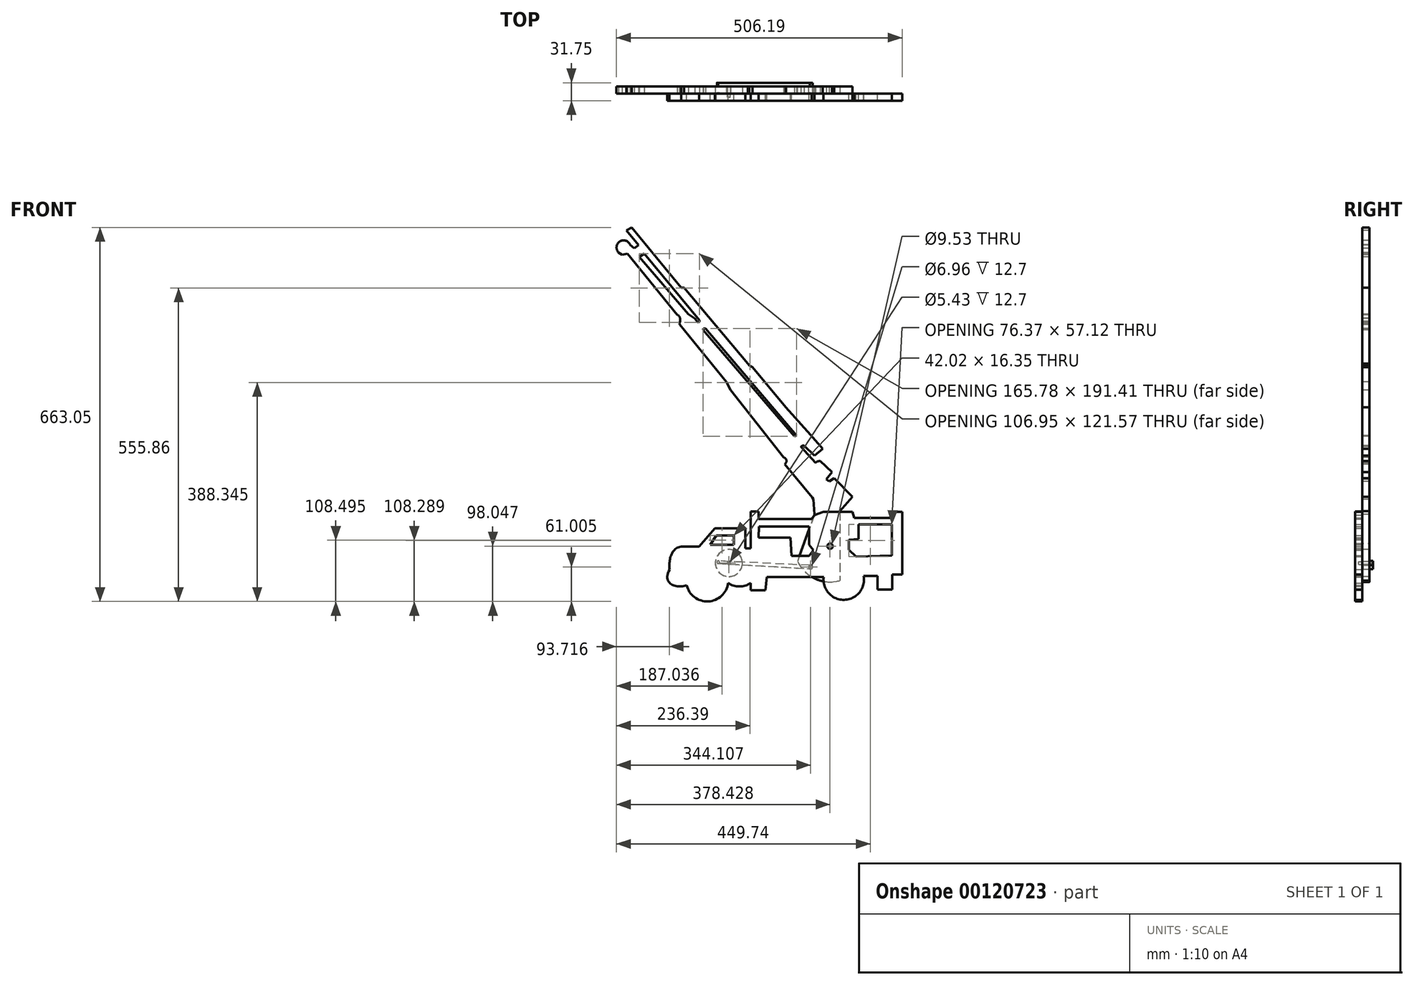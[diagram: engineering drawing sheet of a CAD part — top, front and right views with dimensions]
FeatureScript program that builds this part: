
annotation { "Feature Type Name" : "Feature", "Feature Type Description" : "" }
export const myFeature = defineFeature(function(context is Context, id is Id, definition is map)
    precondition{}
    {
        {
            var Q0;
            Q0=qCreatedBy(makeId("Front.planeOp"),FACE);
            var sketch = newSketch(context, id + "F0", { "sketchPlane" : qUnion([Q0])});
            skLineSegment(sketch, "E0", {"start": v(-70.97, -268.37) * mm, "end": v(-14.7, -268.37) * mm});
            skLineSegment(sketch, "E1", {"start": v(-14.7, -268.37) * mm, "end": v(-12.8, -300.2) * mm});
            skLineSegment(sketch, "E2", {"start": v(-12.8, -300.2) * mm, "end": v(18.8, -300.2) * mm});
            skLineSegment(sketch, "E3", {"start": v(18.8, -300.2) * mm, "end": v(25.92, -290.22) * mm});
            skLineSegment(sketch, "E4", {"start": v(25.92, -290.22) * mm, "end": v(18.8, -280.72) * mm});
            skLineSegment(sketch, "E5", {"start": v(18.8, -280.72) * mm, "end": v(18.8, -248.42) * mm});
            skLineSegment(sketch, "E6", {"start": v(18.8, -248.42) * mm, "end": v(-70.5, -248.42) * mm});
            skLineSegment(sketch, "E7", {"start": v(-70.5, -248.42) * mm, "end": v(-70.97, -268.37) * mm});
            skLineSegment(sketch, "E8", {"start": v(-176.17, -284.05) * mm, "end": v(-148.62, -251.27) * mm});
            skLineSegment(sketch, "E9", {"start": v(-148.62, -251.27) * mm, "end": v(-94.72, -251.27) * mm});
            skLineSegment(sketch, "E10", {"start": v(-94.72, -251.27) * mm, "end": v(-94.72, -287.37) * mm});
            skLineSegment(sketch, "E11", {"start": v(-94.72, -287.37) * mm, "end": v(-84.98, -287.37) * mm});
            skLineSegment(sketch, "E12", {"start": v(-84.98, -287.37) * mm, "end": v(-84.98, -221.83) * mm});
            skLineSegment(sketch, "E13", {"start": v(-84.98, -221.83) * mm, "end": v(-70.97, -221.83) * mm});
            skLineSegment(sketch, "E14", {"start": v(-70.97, -221.83) * mm, "end": v(-70.97, -234.89) * mm});
            skLineSegment(sketch, "E15", {"start": v(-70.97, -234.89) * mm, "end": v(22.83, -234.89) * mm});
            skLineSegment(sketch, "E16", {"start": v(22.83, -234.89) * mm, "end": v(28.3, -228) * mm});
            skLineSegment(sketch, "E17", {"start": v(28.3, -228) * mm, "end": v(44.2, -222.3) * mm});
            skLineSegment(sketch, "E18", {"start": v(44.2, -222.3) * mm, "end": v(95.5, -222.3) * mm});
            skLineSegment(sketch, "E19", {"start": v(95.5, -222.3) * mm, "end": v(98.58, -233.46) * mm});
            skLineSegment(sketch, "E20", {"start": v(98.58, -233.46) * mm, "end": v(165.08, -233.46) * mm});
            skLineSegment(sketch, "E21", {"start": v(165.08, -233.46) * mm, "end": v(165.08, -222.07) * mm});
            skLineSegment(sketch, "E22", {"start": v(165.08, -222.07) * mm, "end": v(183.43, -222.07) * mm});
            skLineSegment(sketch, "E23", {"start": v(183.43, -222.07) * mm, "end": v(183.43, -333.2) * mm});
            skLineSegment(sketch, "E24", {"start": v(183.43, -333.2) * mm, "end": v(165.79, -333.2) * mm});
            skLineSegment(sketch, "E25", {"start": v(165.79, -333.2) * mm, "end": v(165.79, -360.27) * mm});
            skLineSegment(sketch, "E26", {"start": v(165.79, -360.27) * mm, "end": v(139.9, -360.27) * mm});
            skLineSegment(sketch, "E27", {"start": v(139.9, -360.27) * mm, "end": v(139.9, -336.29) * mm});
            skLineSegment(sketch, "E28", {"start": v(139.9, -336.29) * mm, "end": v(115.2, -336.29) * mm});
            skLineSegment(sketch, "E29", {"start": v(44.44, -338.19) * mm, "end": v(-56.49, -338.19) * mm});
            skLineSegment(sketch, "E30", {"start": v(-56.49, -338.19) * mm, "end": v(-58.86, -361.43) * mm});
            skLineSegment(sketch, "E31", {"start": v(-58.86, -361.43) * mm, "end": v(-85.03, -361.43) * mm});
            skLineSegment(sketch, "E32", {"start": v(-85.03, -361.43) * mm, "end": v(-85.03, -348.85) * mm});
            skLineSegment(sketch, "E33", {"start": v(-208.06, -283.94) * mm, "end": v(-176.17, -284.05) * mm});
            skLineSegment(sketch, "E34", {"start": v(-156.73, -280.67) * mm, "end": v(-146.16, -264.57) * mm});
            skLineSegment(sketch, "E35", {"start": v(-146.16, -264.57) * mm, "end": v(-114.72, -264.57) * mm});
            skLineSegment(sketch, "E36", {"start": v(-114.72, -264.57) * mm, "end": v(-114.72, -280.92) * mm});
            skLineSegment(sketch, "E37", {"start": v(-114.72, -280.92) * mm, "end": v(-156.73, -280.67) * mm});
            skLineSegment(sketch, "E38", {"start": v(165.17, -244.4) * mm, "end": v(165.17, -299.82) * mm});
            skLineSegment(sketch, "E39", {"start": v(165.17, -299.82) * mm, "end": v(101.49, -301.51) * mm});
            skLineSegment(sketch, "E40", {"start": v(101.49, -301.51) * mm, "end": v(88.8, -289.45) * mm});
            skLineSegment(sketch, "E41", {"start": v(88.8, -289.45) * mm, "end": v(88.8, -272.1) * mm});
            skLineSegment(sketch, "E42", {"start": v(88.8, -272.1) * mm, "end": v(106.14, -270.41) * mm});
            skLineSegment(sketch, "E43", {"start": v(106.14, -270.41) * mm, "end": v(106.14, -244.4) * mm});
            skLineSegment(sketch, "E44", {"start": v(106.14, -244.4) * mm, "end": v(165.17, -244.4) * mm});
            skArc(sketch, "E45", {"start": v(44.44, -338.19) * mm, "mid": v(80.93, -378.42) * mm, "end": v(115.2, -336.29) * mm});
            skArc(sketch, "E46", {"start": v(-199, -348.85) * mm, "mid": v(-162.01, -381.24) * mm, "end": v(-125.03, -348.85) * mm});
            skArc(sketch, "E47", {"start": v(-125.03, -348.85) * mm, "mid": v(-105.03, -354.54) * mm, "end": v(-85.03, -348.85) * mm});
            skFitSpline(sketch, "E48", {"points": [v(-208.06, -283.94) * mm, v(-228.69, -324.45) * mm], "startDerivative": vector(-59.8, -8.02) * mm, "endDerivative": vector(5.3, -34.5) * mm});
            skFitSpline(sketch, "E49", {"points": [v(-198.37, -352.3) * mm, v(-228.69, -324.45) * mm], "startDerivative": vector(-50.07, -20.1) * mm, "endDerivative": vector(43.3, 82.5) * mm});
            skLineSegment(sketch, "E50", {"start": v(-305.5, 276.53) * mm, "end": v(-295.52, 281.81) * mm});
            skLineSegment(sketch, "E51", {"start": v(-295.52, 281.81) * mm, "end": v(-208.1, 175.03) * mm});
            skLineSegment(sketch, "E52", {"start": v(-208.1, 175.03) * mm, "end": v(-203.24, 175.03) * mm});
            skLineSegment(sketch, "E53", {"start": v(-203.24, 175.03) * mm, "end": v(-90.29, 40.23) * mm});
            skLineSegment(sketch, "E54", {"start": v(-90.29, 40.23) * mm, "end": v(-87.44, 37.62) * mm});
            skLineSegment(sketch, "E55", {"start": v(-87.44, 37.62) * mm, "end": v(-81.5, 34.05) * mm});
            skLineSegment(sketch, "E56", {"start": v(-81.5, 34.05) * mm, "end": v(-22.51, -37.08) * mm});
            skLineSegment(sketch, "E57", {"start": v(-22.51, -37.08) * mm, "end": v(20.91, -85.9) * mm});
            skLineSegment(sketch, "E58", {"start": v(20.91, -85.9) * mm, "end": v(42.79, -110.3) * mm});
            skLineSegment(sketch, "E59", {"start": v(42.79, -110.3) * mm, "end": v(27.97, -122.45) * mm});
            skLineSegment(sketch, "E60", {"start": v(27.97, -122.45) * mm, "end": v(9.4, -104.62) * mm});
            skLineSegment(sketch, "E61", {"start": v(9.4, -104.62) * mm, "end": v(4.22, -107) * mm});
            skLineSegment(sketch, "E62", {"start": v(4.22, -107) * mm, "end": v(29.81, -135.31) * mm});
            skLineSegment(sketch, "E63", {"start": v(38.4, -132.45) * mm, "end": v(59.47, -152.17) * mm});
            skLineSegment(sketch, "E64", {"start": v(59.47, -152.17) * mm, "end": v(49.15, -164.34) * mm});
            skLineSegment(sketch, "E65", {"start": v(49.15, -164.34) * mm, "end": v(54.1, -168.54) * mm});
            skLineSegment(sketch, "E66", {"start": v(54.1, -168.54) * mm, "end": v(63.2, -162.72) * mm});
            skLineSegment(sketch, "E67", {"start": v(63.2, -162.72) * mm, "end": v(95.33, -195.57) * mm});
            skLineSegment(sketch, "E68", {"start": v(95.33, -195.57) * mm, "end": v(72.9, -221.17) * mm});
            skLineSegment(sketch, "E69", {"start": v(72.9, -221.17) * mm, "end": v(43.7, -221.17) * mm});
            skLineSegment(sketch, "E70", {"start": v(43.7, -221.17) * mm, "end": v(28.16, -226.67) * mm});
            skLineSegment(sketch, "E71", {"start": v(28.16, -226.67) * mm, "end": v(26.25, -200.01) * mm});
            skLineSegment(sketch, "E72", {"start": v(26.25, -200.01) * mm, "end": v(24.24, -197.16) * mm});
            skLineSegment(sketch, "E73", {"start": v(24.24, -197.16) * mm, "end": v(-24.88, -137.93) * mm});
            skLineSegment(sketch, "E74", {"start": v(-26.67, -125.71) * mm, "end": v(-120.23, -6.25) * mm});
            skLineSegment(sketch, "E75", {"start": v(-120.23, -6.25) * mm, "end": v(-128.07, 7.99) * mm});
            skLineSegment(sketch, "E76", {"start": v(-128.07, 7.99) * mm, "end": v(-210.4, 110.04) * mm});
            skLineSegment(sketch, "E77", {"start": v(-210.4, 110.04) * mm, "end": v(-211, 112.1) * mm});
            skLineSegment(sketch, "E78", {"start": v(-211, 112.1) * mm, "end": v(-210.26, 115.3) * mm});
            skLineSegment(sketch, "E79", {"start": v(-210.26, 115.3) * mm, "end": v(-210.26, 121.03) * mm});
            skLineSegment(sketch, "E80", {"start": v(-214.9, 127.1) * mm, "end": v(-303.36, 235.3) * mm});
            skLineSegment(sketch, "E81", {"start": v(-303.36, 235.3) * mm, "end": v(-312.78, 233.5) * mm});
            skLineSegment(sketch, "E82", {"start": v(-312.78, 233.5) * mm, "end": v(-319.05, 237.54) * mm});
            skLineSegment(sketch, "E83", {"start": v(-298.66, 251.66) * mm, "end": v(-291.04, 244.71) * mm});
            skLineSegment(sketch, "E84", {"start": v(-291.04, 244.71) * mm, "end": v(-283.64, 250.54) * mm});
            skLineSegment(sketch, "E85", {"start": v(-283.64, 250.54) * mm, "end": v(-305.5, 276.53) * mm});
            skLineSegment(sketch, "E86", {"start": v(-282.52, 230.03) * mm, "end": v(-273.33, 235.4) * mm});
            skLineSegment(sketch, "E87", {"start": v(-273.33, 235.4) * mm, "end": v(-176.05, 117.36) * mm});
            skLineSegment(sketch, "E88", {"start": v(-179.39, 114.6) * mm, "end": v(-184.03, 120.25) * mm});
            skLineSegment(sketch, "E89", {"start": v(-184.03, 120.25) * mm, "end": v(-195.62, 127.85) * mm});
            skLineSegment(sketch, "E90", {"start": v(-195.62, 127.85) * mm, "end": v(-282.52, 230.03) * mm});
            skLineSegment(sketch, "E91", {"start": v(-165.1, 102.8) * mm, "end": v(-3.48, -87.22) * mm});
            skLineSegment(sketch, "E92", {"start": v(-3.48, -87.22) * mm, "end": v(-7.74, -88.6) * mm});
            skLineSegment(sketch, "E93", {"start": v(-7.74, -88.6) * mm, "end": v(-169.26, 100.29) * mm});
            skLineSegment(sketch, "E94", {"start": v(-169.26, 100.29) * mm, "end": v(-168.67, 102.8) * mm});
            skLineSegment(sketch, "E95", {"start": v(-168.67, 102.8) * mm, "end": v(-165.1, 102.8) * mm});
            skArc(sketch, "E96", {"start": v(-24.88, -137.93) * mm, "mid": v(-21.64, -131.22) * mm, "end": v(-26.67, -125.71) * mm});
            skArc(sketch, "E97", {"start": v(38.4, -132.45) * mm, "mid": v(33.76, -132.83) * mm, "end": v(29.81, -135.31) * mm});
            skArc(sketch, "E98", {"start": v(9.4, -104.62) * mm, "mid": v(6.53, -105.2) * mm, "end": v(4.22, -107) * mm});
            skArc(sketch, "E99", {"start": v(-179.39, 114.6) * mm, "mid": v(-176.35, 114.32) * mm, "end": v(-176.05, 117.36) * mm});
            skArc(sketch, "E100", {"start": v(-210.26, 121.03) * mm, "mid": v(-211.84, 124.63) * mm, "end": v(-214.9, 127.1) * mm});
            skArc(sketch, "E101", {"start": v(-298.66, 251.66) * mm, "mid": v(-317.33, 256.85) * mm, "end": v(-319.05, 237.54) * mm});
            skSolve(sketch);
        }
        {
            var Q0;
            Q0=makeQuery(id+"F0.imprint","IMPRINT",FACE,{"disambiguationData":[TD([[makeQuery(id+"F0.imprint","IMPRINT",EDGE,{"derivedFrom":sQuery(id+"F0.wireOp",EDGE,"E0")}),-1.0]])]});
            extrude(context, id + "F1", {"entities" : qUnion([Q0]), "depth" : 12.7 * mm});
        }
        {
            var Q0;
            Q0=makeQuery(id+"F0.imprint","IMPRINT",FACE,{"disambiguationData":[TD([[makeQuery(id+"F0.imprint","IMPRINT",EDGE,{"derivedFrom":sQuery(id+"F0.wireOp",EDGE,"E50")}),-1.0]])]});
            extrude(context, id + "F2", {"entities" : qUnion([Q0]), "oppositeDirection" : true, "depth" : 12.7 * mm});
        }
        {
            var Q0;
            Q0=makeQuery(id+"F2.opExtrude","CAP_FACE",FACE,{"disambiguationData":[OSD([sQuery(id+"F0.wireOp",EDGE,"E50"),sQuery(id+"F0.wireOp",EDGE,"E51"),sQuery(id+"F0.wireOp",EDGE,"E52"),sQuery(id+"F0.wireOp",EDGE,"E53"),sQuery(id+"F0.wireOp",EDGE,"E54"),sQuery(id+"F0.wireOp",EDGE,"E55"),sQuery(id+"F0.wireOp",EDGE,"E56"),sQuery(id+"F0.wireOp",EDGE,"E57"),sQuery(id+"F0.wireOp",EDGE,"E58"),sQuery(id+"F0.wireOp",EDGE,"E59"),sQuery(id+"F0.wireOp",EDGE,"E60"),sQuery(id+"F0.wireOp",EDGE,"E62"),sQuery(id+"F0.wireOp",EDGE,"E63"),sQuery(id+"F0.wireOp",EDGE,"E64"),sQuery(id+"F0.wireOp",EDGE,"E65"),sQuery(id+"F0.wireOp",EDGE,"E66"),sQuery(id+"F0.wireOp",EDGE,"E67"),sQuery(id+"F0.wireOp",EDGE,"E68"),sQuery(id+"F0.wireOp",EDGE,"E69"),sQuery(id+"F0.wireOp",EDGE,"E70"),sQuery(id+"F0.wireOp",EDGE,"E71"),sQuery(id+"F0.wireOp",EDGE,"E72"),sQuery(id+"F0.wireOp",EDGE,"E73"),sQuery(id+"F0.wireOp",EDGE,"E74"),sQuery(id+"F0.wireOp",EDGE,"E75"),sQuery(id+"F0.wireOp",EDGE,"E76"),sQuery(id+"F0.wireOp",EDGE,"E77"),sQuery(id+"F0.wireOp",EDGE,"E78"),sQuery(id+"F0.wireOp",EDGE,"E79"),sQuery(id+"F0.wireOp",EDGE,"E80"),sQuery(id+"F0.wireOp",EDGE,"E81"),sQuery(id+"F0.wireOp",EDGE,"E82"),sQuery(id+"F0.wireOp",EDGE,"E83"),sQuery(id+"F0.wireOp",EDGE,"E84"),sQuery(id+"F0.wireOp",EDGE,"E85"),sQuery(id+"F0.wireOp",EDGE,"E86"),sQuery(id+"F0.wireOp",EDGE,"E87"),sQuery(id+"F0.wireOp",EDGE,"E88"),sQuery(id+"F0.wireOp",EDGE,"E89"),sQuery(id+"F0.wireOp",EDGE,"E90"),sQuery(id+"F0.wireOp",EDGE,"E91"),sQuery(id+"F0.wireOp",EDGE,"E92"),sQuery(id+"F0.wireOp",EDGE,"E93"),sQuery(id+"F0.wireOp",EDGE,"E94"),sQuery(id+"F0.wireOp",EDGE,"E95"),sQuery(id+"F0.wireOp",EDGE,"E96"),sQuery(id+"F0.wireOp",EDGE,"E97"),sQuery(id+"F0.wireOp",EDGE,"E98"),sQuery(id+"F0.wireOp",EDGE,"E99"),sQuery(id+"F0.wireOp",EDGE,"E100"),sQuery(id+"F0.wireOp",EDGE,"E101")])],"isStart":false});
            var sketch = newSketch(context, id + "F3", { "sketchPlane" : qUnion([Q0])});
            skArc(sketch, "E102", {"start": v(-72.9, -344.3) * mm, "mid": v(-29.24, -340.93) * mm, "end": v(1.86, -310.08) * mm});
            skLineSegment(sketch, "E103", {"start": v(-72.9, -221.17) * mm, "end": v(-72.9, -344.3) * mm});
            skLineSegment(sketch, "E104", {"start": v(-28.16, -226.67) * mm, "end": v(1.86, -310.08) * mm});
            skSolve(sketch);
        }
        {
            var Q0;
            Q0=makeQuery(id+"F3.imprint","IMPRINT",FACE,{"disambiguationData":[TD([[makeQuery(id+"F3.imprint","IMPRINT",EDGE,{"derivedFrom":sQuery(id+"F3.wireOp",EDGE,"E102")}),1.0]])]});
            extrude(context, id + "F4", {"entities" : qUnion([Q0]), "operationType" : NewBodyOperationType.ADD, "oppositeDirection" : true, "depth" : 12.7 * mm});
        }
        {
            var Q0;
            Q0=makeQuery(id+"F4.boolean.opBoolean","MERGE",FACE,{"derivedFrom":[makeQuery(id+"F2.opExtrude","CAP_FACE",FACE,{"disambiguationData":[OSD([sQuery(id+"F0.wireOp",EDGE,"E50"),sQuery(id+"F0.wireOp",EDGE,"E51"),sQuery(id+"F0.wireOp",EDGE,"E52"),sQuery(id+"F0.wireOp",EDGE,"E53"),sQuery(id+"F0.wireOp",EDGE,"E54"),sQuery(id+"F0.wireOp",EDGE,"E55"),sQuery(id+"F0.wireOp",EDGE,"E56"),sQuery(id+"F0.wireOp",EDGE,"E57"),sQuery(id+"F0.wireOp",EDGE,"E58"),sQuery(id+"F0.wireOp",EDGE,"E59"),sQuery(id+"F0.wireOp",EDGE,"E60"),sQuery(id+"F0.wireOp",EDGE,"E62"),sQuery(id+"F0.wireOp",EDGE,"E63"),sQuery(id+"F0.wireOp",EDGE,"E64"),sQuery(id+"F0.wireOp",EDGE,"E65"),sQuery(id+"F0.wireOp",EDGE,"E66"),sQuery(id+"F0.wireOp",EDGE,"E67"),sQuery(id+"F0.wireOp",EDGE,"E68"),sQuery(id+"F0.wireOp",EDGE,"E69"),sQuery(id+"F0.wireOp",EDGE,"E70"),sQuery(id+"F0.wireOp",EDGE,"E71"),sQuery(id+"F0.wireOp",EDGE,"E72"),sQuery(id+"F0.wireOp",EDGE,"E73"),sQuery(id+"F0.wireOp",EDGE,"E74"),sQuery(id+"F0.wireOp",EDGE,"E75"),sQuery(id+"F0.wireOp",EDGE,"E76"),sQuery(id+"F0.wireOp",EDGE,"E77"),sQuery(id+"F0.wireOp",EDGE,"E78"),sQuery(id+"F0.wireOp",EDGE,"E79"),sQuery(id+"F0.wireOp",EDGE,"E80"),sQuery(id+"F0.wireOp",EDGE,"E81"),sQuery(id+"F0.wireOp",EDGE,"E82"),sQuery(id+"F0.wireOp",EDGE,"E83"),sQuery(id+"F0.wireOp",EDGE,"E84"),sQuery(id+"F0.wireOp",EDGE,"E85"),sQuery(id+"F0.wireOp",EDGE,"E86"),sQuery(id+"F0.wireOp",EDGE,"E87"),sQuery(id+"F0.wireOp",EDGE,"E88"),sQuery(id+"F0.wireOp",EDGE,"E89"),sQuery(id+"F0.wireOp",EDGE,"E90"),sQuery(id+"F0.wireOp",EDGE,"E91"),sQuery(id+"F0.wireOp",EDGE,"E92"),sQuery(id+"F0.wireOp",EDGE,"E93"),sQuery(id+"F0.wireOp",EDGE,"E94"),sQuery(id+"F0.wireOp",EDGE,"E95"),sQuery(id+"F0.wireOp",EDGE,"E96"),sQuery(id+"F0.wireOp",EDGE,"E97"),sQuery(id+"F0.wireOp",EDGE,"E98"),sQuery(id+"F0.wireOp",EDGE,"E99"),sQuery(id+"F0.wireOp",EDGE,"E100"),sQuery(id+"F0.wireOp",EDGE,"E101")])],"isStart":false}),makeQuery(id+"F4.opExtrude","CAP_FACE",FACE,{"disambiguationData":[OSD([sQuery(id+"F3.wireOp",EDGE,"E102")])],"isStart":true})]});
            var sketch = newSketch(context, id + "F5", { "sketchPlane" : qUnion([Q0])});
            skCircle(sketch, "E105", {"center": v(-55.67, -283.2) * mm, "radius": 4.76 * mm});
            skSolve(sketch);
        }
        {
            var Q0;
            Q0=makeQuery(id+"F5.imprint","IMPRINT",FACE,{"disambiguationData":[TD([[makeQuery(id+"F5.imprint","IMPRINT",EDGE,{"derivedFrom":sQuery(id+"F5.wireOp",EDGE,"E105")}),1.0]])]});
            extrude(context, id + "F6", {"entities" : qUnion([Q0]), "operationType" : NewBodyOperationType.REMOVE, "endBound" : BoundingType.THROUGH_ALL, "oppositeDirection" : true, "depth" : 25.4 * mm});
        }
        {
            var Q0;
            Q0=makeQuery(id+"F0.imprint","IMPRINT",FACE,{"disambiguationData":[TD([[makeQuery(id+"F0.imprint","IMPRINT",EDGE,{"derivedFrom":sQuery(id+"F0.wireOp",EDGE,"E0")}),-1.0]])]});
            var sketch = newSketch(context, id + "F7", { "sketchPlane" : qUnion([Q0])});
            skCircle(sketch, "E106", {"center": v(-123.63, -313.1) * mm, "radius": 23.99 * mm});
            skCircle(sketch, "E107", {"center": v(-142.63, -311.68) * mm, "radius": 2.24 * mm});
            skCircle(sketch, "E108", {"center": v(-123.63, -313.1) * mm, "radius": 2.71 * mm});
            skSolve(sketch);
        }
        {
            var Q0;
            Q0 = qSketchRegion(id + "F7", true);
            extrude(context, id + "F8", {"entities" : qUnion([Q0]), "oppositeDirection" : true, "depth" : 12.7 * mm});
        }
        {
            var Q0;
            Q0=makeQuery(id+"F7.imprint","IMPRINT",FACE,{"disambiguationData":[TD([[makeQuery(id+"F7.imprint","IMPRINT",EDGE,{"derivedFrom":sQuery(id+"F7.wireOp",EDGE,"E108")}),1.0]])]});
            extrude(context, id + "F9", {"entities" : qUnion([Q0]), "operationType" : NewBodyOperationType.REMOVE, "depth" : 6.35 * mm});
        }
        {
            var Q0;
            Q0=makeQuery(id+"F4.boolean.opBoolean","MERGE",FACE,{"derivedFrom":[makeQuery(id+"F2.opExtrude","CAP_FACE",FACE,{"disambiguationData":[OSD([sQuery(id+"F0.wireOp",EDGE,"E50"),sQuery(id+"F0.wireOp",EDGE,"E51"),sQuery(id+"F0.wireOp",EDGE,"E52"),sQuery(id+"F0.wireOp",EDGE,"E53"),sQuery(id+"F0.wireOp",EDGE,"E54"),sQuery(id+"F0.wireOp",EDGE,"E55"),sQuery(id+"F0.wireOp",EDGE,"E56"),sQuery(id+"F0.wireOp",EDGE,"E57"),sQuery(id+"F0.wireOp",EDGE,"E58"),sQuery(id+"F0.wireOp",EDGE,"E59"),sQuery(id+"F0.wireOp",EDGE,"E60"),sQuery(id+"F0.wireOp",EDGE,"E62"),sQuery(id+"F0.wireOp",EDGE,"E63"),sQuery(id+"F0.wireOp",EDGE,"E64"),sQuery(id+"F0.wireOp",EDGE,"E65"),sQuery(id+"F0.wireOp",EDGE,"E66"),sQuery(id+"F0.wireOp",EDGE,"E67"),sQuery(id+"F0.wireOp",EDGE,"E68"),sQuery(id+"F0.wireOp",EDGE,"E69"),sQuery(id+"F0.wireOp",EDGE,"E70"),sQuery(id+"F0.wireOp",EDGE,"E71"),sQuery(id+"F0.wireOp",EDGE,"E72"),sQuery(id+"F0.wireOp",EDGE,"E73"),sQuery(id+"F0.wireOp",EDGE,"E74"),sQuery(id+"F0.wireOp",EDGE,"E75"),sQuery(id+"F0.wireOp",EDGE,"E76"),sQuery(id+"F0.wireOp",EDGE,"E77"),sQuery(id+"F0.wireOp",EDGE,"E78"),sQuery(id+"F0.wireOp",EDGE,"E79"),sQuery(id+"F0.wireOp",EDGE,"E80"),sQuery(id+"F0.wireOp",EDGE,"E81"),sQuery(id+"F0.wireOp",EDGE,"E82"),sQuery(id+"F0.wireOp",EDGE,"E83"),sQuery(id+"F0.wireOp",EDGE,"E84"),sQuery(id+"F0.wireOp",EDGE,"E85"),sQuery(id+"F0.wireOp",EDGE,"E86"),sQuery(id+"F0.wireOp",EDGE,"E87"),sQuery(id+"F0.wireOp",EDGE,"E88"),sQuery(id+"F0.wireOp",EDGE,"E89"),sQuery(id+"F0.wireOp",EDGE,"E90"),sQuery(id+"F0.wireOp",EDGE,"E91"),sQuery(id+"F0.wireOp",EDGE,"E92"),sQuery(id+"F0.wireOp",EDGE,"E93"),sQuery(id+"F0.wireOp",EDGE,"E94"),sQuery(id+"F0.wireOp",EDGE,"E95"),sQuery(id+"F0.wireOp",EDGE,"E96"),sQuery(id+"F0.wireOp",EDGE,"E97"),sQuery(id+"F0.wireOp",EDGE,"E98"),sQuery(id+"F0.wireOp",EDGE,"E99"),sQuery(id+"F0.wireOp",EDGE,"E100"),sQuery(id+"F0.wireOp",EDGE,"E101")])],"isStart":false}),makeQuery(id+"F4.opExtrude","CAP_FACE",FACE,{"disambiguationData":[OSD([sQuery(id+"F3.wireOp",EDGE,"E102")])],"isStart":true})]});
            var sketch = newSketch(context, id + "F10", { "sketchPlane" : qUnion([Q0])});
            skCircle(sketch, "E109", {"center": v(-21.35, -320.23) * mm, "radius": 3.48 * mm});
            skSolve(sketch);
        }
        {
            var Q0;
            Q0=makeQuery(id+"F10.imprint","IMPRINT",FACE,{"disambiguationData":[TD([[makeQuery(id+"F10.imprint","IMPRINT",EDGE,{"derivedFrom":sQuery(id+"F10.wireOp",EDGE,"E109")}),1.0]])]});
            extrude(context, id + "F11", {"entities" : qUnion([Q0]), "operationType" : NewBodyOperationType.REMOVE, "oppositeDirection" : true, "depth" : 12.7 * mm});
        }
        {
            var Q0;
            Q0=makeQuery(id+"F4.boolean.opBoolean","MERGE",FACE,{"derivedFrom":[makeQuery(id+"F2.opExtrude","CAP_FACE",FACE,{"disambiguationData":[OSD([sQuery(id+"F0.wireOp",EDGE,"E50"),sQuery(id+"F0.wireOp",EDGE,"E51"),sQuery(id+"F0.wireOp",EDGE,"E52"),sQuery(id+"F0.wireOp",EDGE,"E53"),sQuery(id+"F0.wireOp",EDGE,"E54"),sQuery(id+"F0.wireOp",EDGE,"E55"),sQuery(id+"F0.wireOp",EDGE,"E56"),sQuery(id+"F0.wireOp",EDGE,"E57"),sQuery(id+"F0.wireOp",EDGE,"E58"),sQuery(id+"F0.wireOp",EDGE,"E59"),sQuery(id+"F0.wireOp",EDGE,"E60"),sQuery(id+"F0.wireOp",EDGE,"E62"),sQuery(id+"F0.wireOp",EDGE,"E63"),sQuery(id+"F0.wireOp",EDGE,"E64"),sQuery(id+"F0.wireOp",EDGE,"E65"),sQuery(id+"F0.wireOp",EDGE,"E66"),sQuery(id+"F0.wireOp",EDGE,"E67"),sQuery(id+"F0.wireOp",EDGE,"E68"),sQuery(id+"F0.wireOp",EDGE,"E69"),sQuery(id+"F0.wireOp",EDGE,"E70"),sQuery(id+"F0.wireOp",EDGE,"E71"),sQuery(id+"F0.wireOp",EDGE,"E72"),sQuery(id+"F0.wireOp",EDGE,"E73"),sQuery(id+"F0.wireOp",EDGE,"E74"),sQuery(id+"F0.wireOp",EDGE,"E75"),sQuery(id+"F0.wireOp",EDGE,"E76"),sQuery(id+"F0.wireOp",EDGE,"E77"),sQuery(id+"F0.wireOp",EDGE,"E78"),sQuery(id+"F0.wireOp",EDGE,"E79"),sQuery(id+"F0.wireOp",EDGE,"E80"),sQuery(id+"F0.wireOp",EDGE,"E81"),sQuery(id+"F0.wireOp",EDGE,"E82"),sQuery(id+"F0.wireOp",EDGE,"E83"),sQuery(id+"F0.wireOp",EDGE,"E84"),sQuery(id+"F0.wireOp",EDGE,"E85"),sQuery(id+"F0.wireOp",EDGE,"E86"),sQuery(id+"F0.wireOp",EDGE,"E87"),sQuery(id+"F0.wireOp",EDGE,"E88"),sQuery(id+"F0.wireOp",EDGE,"E89"),sQuery(id+"F0.wireOp",EDGE,"E90"),sQuery(id+"F0.wireOp",EDGE,"E91"),sQuery(id+"F0.wireOp",EDGE,"E92"),sQuery(id+"F0.wireOp",EDGE,"E93"),sQuery(id+"F0.wireOp",EDGE,"E94"),sQuery(id+"F0.wireOp",EDGE,"E95"),sQuery(id+"F0.wireOp",EDGE,"E96"),sQuery(id+"F0.wireOp",EDGE,"E97"),sQuery(id+"F0.wireOp",EDGE,"E98"),sQuery(id+"F0.wireOp",EDGE,"E99"),sQuery(id+"F0.wireOp",EDGE,"E100"),sQuery(id+"F0.wireOp",EDGE,"E101")])],"isStart":false}),makeQuery(id+"F4.opExtrude","CAP_FACE",FACE,{"disambiguationData":[OSD([sQuery(id+"F3.wireOp",EDGE,"E102")])],"isStart":true})]});
            var sketch = newSketch(context, id + "F12", { "sketchPlane" : qUnion([Q0])});
            skLineSegment(sketch, "E110", {"start": v(-19.8, -317.12) * mm, "end": v(142.44, -309.45) * mm});
            skLineSegment(sketch, "E111", {"start": v(142.83, -313.92) * mm, "end": v(-19.47, -323.16) * mm});
            skArc(sketch, "E112.0", {"start": v(-19.8, -317.12) * mm, "mid": v(-24.82, -320.42) * mm, "end": v(-19.47, -323.16) * mm});
            skArc(sketch, "E113.0", {"start": v(142.44, -309.45) * mm, "mid": v(144.86, -311.5) * mm, "end": v(142.83, -313.92) * mm});
            skSolve(sketch);
        }
        {
            var Q0;
            Q0 = qSketchRegion(id + "F12", true);
            extrude(context, id + "F13", {"entities" : qUnion([Q0]), "depth" : 6.35 * mm});
        }
        {
            var Q0;
            Q0=makeQuery(id+"F13.opExtrude","CAP_FACE",FACE,{"disambiguationData":[OSD([sQuery(id+"F12.wireOp",EDGE,"E110"),sQuery(id+"F12.wireOp",EDGE,"E111"),sQuery(id+"F12.wireOp",EDGE,"E112.0"),sQuery(id+"F12.wireOp",EDGE,"E113.0")])],"isStart":true});
            var sketch = newSketch(context, id + "F14", { "sketchPlane" : qUnion([Q0])});
            skCircle(sketch, "E114", {"center": v(-142.63, -311.68) * mm, "radius": 2.78 * mm});
            skCircle(sketch, "E115", {"center": v(21.35, -320.23) * mm, "radius": 3.42 * mm});
            skSolve(sketch);
        }
        {
            var Q0;
            Q0=makeQuery(id+"F14.imprint","IMPRINT",FACE,{"disambiguationData":[TD([[makeQuery(id+"F14.imprint","IMPRINT",EDGE,{"derivedFrom":sQuery(id+"F14.wireOp",EDGE,"E115")}),1.0]])]});
            var Q1;
            Q1=makeQuery(id+"F14.imprint","IMPRINT",FACE,{"disambiguationData":[TD([[makeQuery(id+"F14.imprint","IMPRINT",EDGE,{"derivedFrom":sQuery(id+"F14.wireOp",EDGE,"E114")}),1.0]])]});
            extrude(context, id + "F15", {"entities" : qUnion([Q0, Q1]), "operationType" : NewBodyOperationType.ADD, "depth" : 11.43 * mm});
        }
    });
